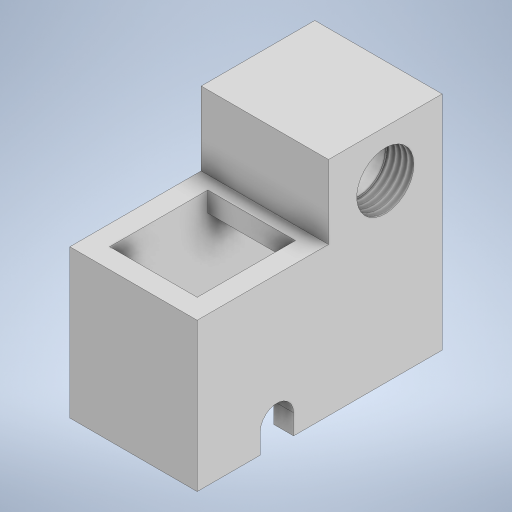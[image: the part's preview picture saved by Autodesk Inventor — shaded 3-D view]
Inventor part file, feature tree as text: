
AUTODESK INVENTOR PART (.ipt)
format: ipt  version: 2024.2 (Build 282272000, 272)  size: 275,968 bytes
history: native  units: in
note: dims shown in document units (in); Inventor stores cm internally (conversion verified against a paired STEP export)
features: sketch x9, extrude x6, hole x2
ambient origin geometry x8: Origin, YZ Plane, XZ Plane, XY Plane, X Axis, Y Axis, Z Axis, Center Point
bodies: Solid1 (feature_tree)
feature tree (17):
  sketch  "Sketch1"  dims[d0=0.5157in d1=1.2087in]
  extrude  "Extrusion1"  Depth=1.2087in
  extrude  "Extrusion2"  Depth=1.4429in
  extrude  "Extrusion3"  Depth=0.1181in TaperAngle=0.0deg
  extrude  "Extrusion5"  Depth=0.1969in TaperAngle=0.0deg
  extrude  "Extrusion6"  Depth=0.1181in
  extrude  "Extrusion7"  TaperAngle=0.0deg  [1 undecoded]
  hole  "Hole1"  [1 undecoded]
  hole  "Hole2"  [1 undecoded]
  sketch  "Sketch2"  dims[d2=0.75in d3=1.4429in]
  sketch  "Sketch3"  dims[d4=0.7559in d5=0.0in d6=0.1181in d7=0.0in]
  sketch  "Sketch4"  dims[d8=0.5787in d9=0.1969in d10=0.0in]
  sketch  "Sketch6"  dims[d16=0.4695in d17=0.1181in]
  sketch  "Sketch7"  dims[d18=0.1969in d19=0.0in d20=0.0in]
  sketch  "Sketch8"  dims[d21=0.6693in d22=0.4331in d23=0.0in]
  sketch  "Sketch9"  dims[d24=0.2756in d25=0.315in]
  sketch  "Sketch10"  dims[d26=0.4331in d27=0.0in d28=0.3372in d29=0.1575in d30=0.1575in d31=0.0787in d32=90.0deg d33=0.1575in d34=0.0in d35=0.3372in d36=0.1575in d37=0.1575in d38=0.0787in d39=90.0deg d40=0.1575in d41=0.0in]
note: 3 required parameter values undecoded (feature->parameter linkage not recoverable at this tier; creation-order binding heuristic only, values carry confidence <= 0.55)
